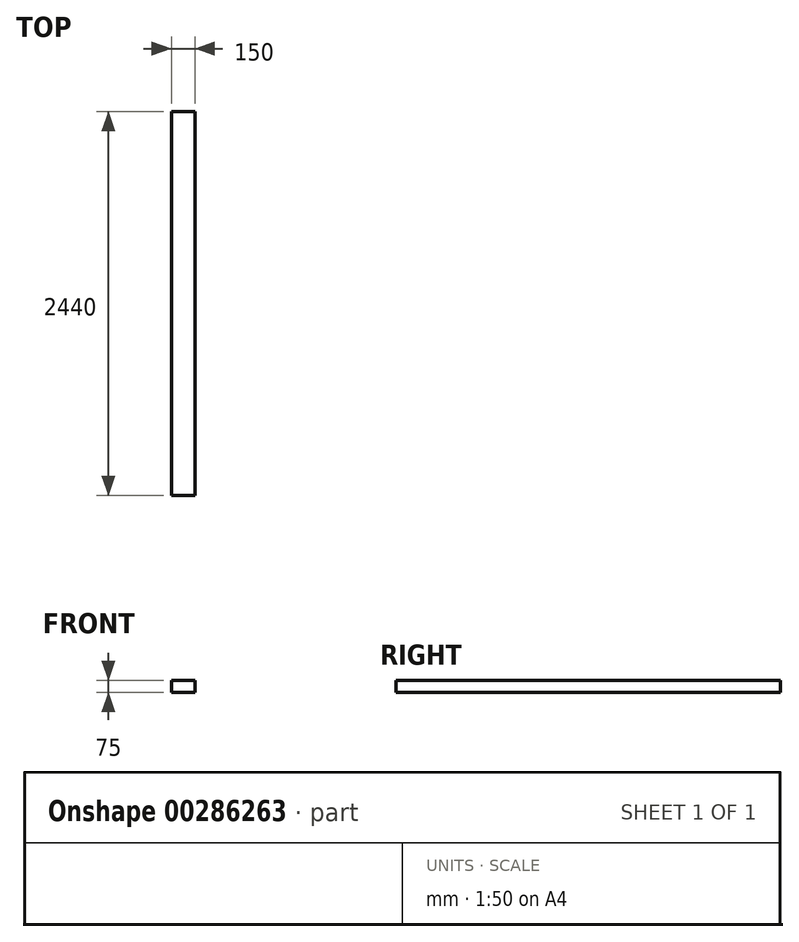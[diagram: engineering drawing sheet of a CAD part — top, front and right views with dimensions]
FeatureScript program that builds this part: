
annotation { "Feature Type Name" : "Feature", "Feature Type Description" : "" }
export const myFeature = defineFeature(function(context is Context, id is Id, definition is map)
    precondition{}
    {
        {
            var Q0;
            Q0=qCreatedBy(makeId("Front.planeOp"),FACE);
            var sketch = newSketch(context, id + "F0", { "sketchPlane" : qUnion([Q0])});
            skLineSegment(sketch, "E0.bottom", {"start": v(-73.78, 37.5) * mm, "end": v(76.22, 37.5) * mm});
            skLineSegment(sketch, "E0.top", {"start": v(-73.78, -37.5) * mm, "end": v(76.22, -37.5) * mm});
            skLineSegment(sketch, "E0.left", {"start": v(-73.78, 37.5) * mm, "end": v(-73.78, -37.5) * mm});
            skLineSegment(sketch, "E0.right", {"start": v(76.22, 37.5) * mm, "end": v(76.22, -37.5) * mm});
            skSolve(sketch);
        }
        {
            var Q0;
            Q0=makeQuery(id+"F0.imprint","IMPRINT",FACE,{"disambiguationData":[TD([[makeQuery(id+"F0.imprint","IMPRINT",EDGE,{"derivedFrom":sQuery(id+"F0.wireOp",EDGE,"E0.bottom")}),-1.0]])]});
            extrude(context, id + "F1", {"entities" : qUnion([Q0]), "depth" : 2440 * mm});
        }
    });
